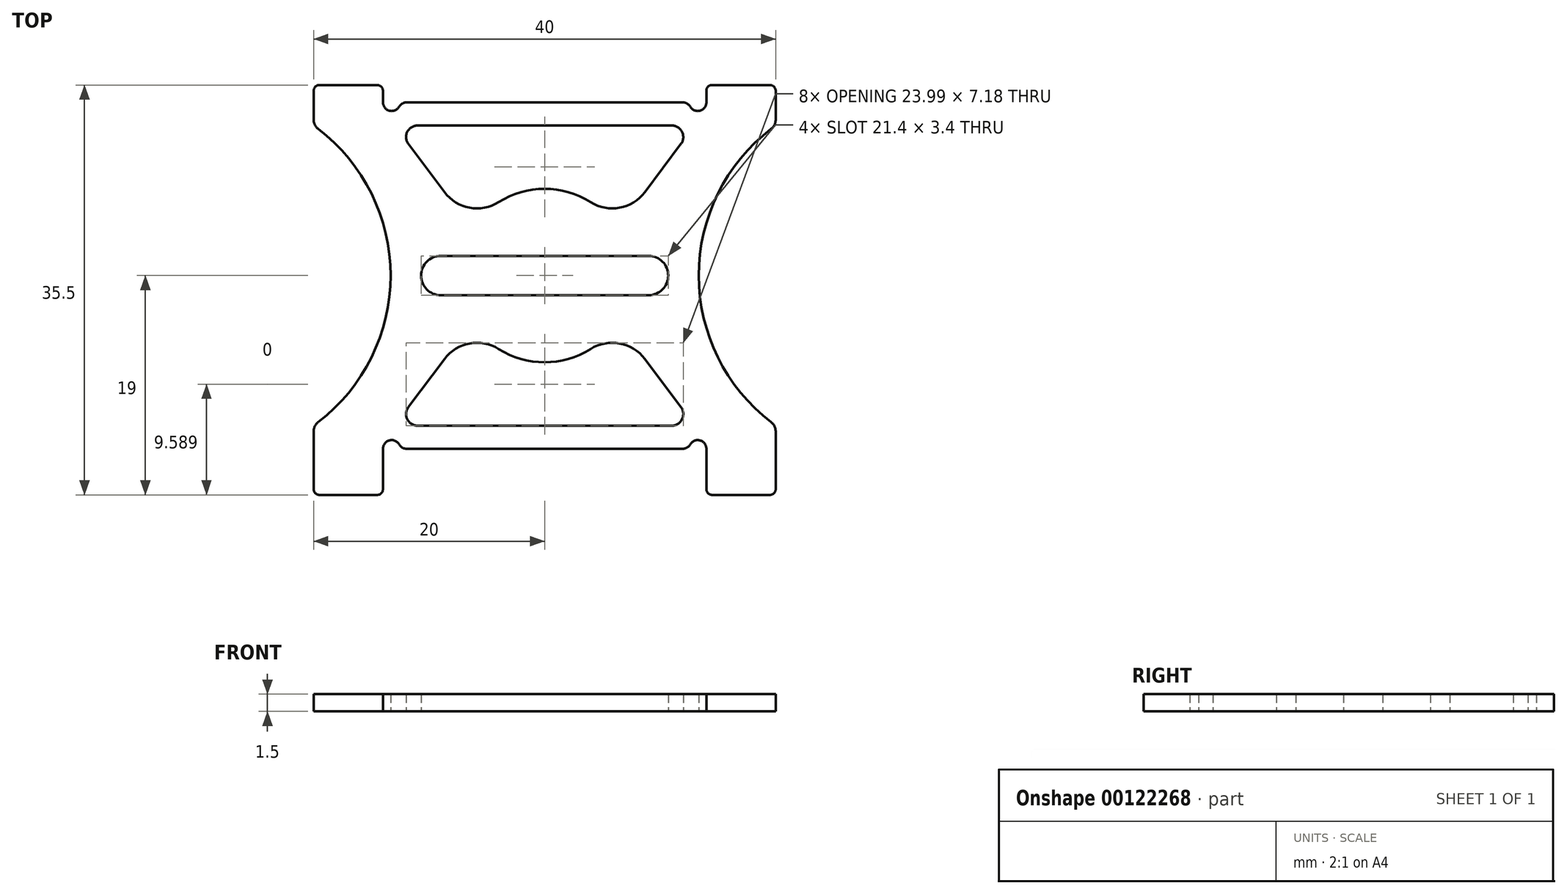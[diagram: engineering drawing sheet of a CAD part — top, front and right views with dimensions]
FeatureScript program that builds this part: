
annotation { "Feature Type Name" : "Feature", "Feature Type Description" : "" }
export const myFeature = defineFeature(function(context is Context, id is Id, definition is map)
    precondition{}
    {
        {
            var Q0;
            Q0=qCreatedBy(makeId("Top.planeOp"),FACE);
            var sketch = newSketch(context, id + "F0", { "sketchPlane" : qUnion([Q0])});
            skArc(sketch, "E0", {"start": v(19.6, 13.95) * mm, "mid": v(19.9, 14.3) * mm, "end": v(20, 14.74) * mm});
            skLineSegment(sketch, "E1", {"start": v(20, 14.74) * mm, "end": v(20, 17.25) * mm});
            skArc(sketch, "E2", {"start": v(20, 17.25) * mm, "mid": v(19.85, 17.6) * mm, "end": v(19.5, 17.75) * mm});
            skLineSegment(sketch, "E3", {"start": v(19.5, 17.75) * mm, "end": v(14.5, 17.75) * mm});
            skArc(sketch, "E4", {"start": v(14.5, 17.75) * mm, "mid": v(14.15, 17.6) * mm, "end": v(14, 17.25) * mm});
            skLineSegment(sketch, "E5", {"start": v(14, 17.25) * mm, "end": v(14, 16.25) * mm});
            skArc(sketch, "E6", {"start": v(12.6, 15.87) * mm, "mid": v(13.44, 15.53) * mm, "end": v(14, 16.25) * mm});
            skArc(sketch, "E7", {"start": v(12.6, 15.88) * mm, "mid": v(12.33, 16.15) * mm, "end": v(11.95, 16.25) * mm});
            skLineSegment(sketch, "E8", {"start": v(11.95, 16.25) * mm, "end": v(-11.95, 16.25) * mm});
            skArc(sketch, "E9", {"start": v(-11.95, 16.25) * mm, "mid": v(-12.33, 16.15) * mm, "end": v(-12.6, 15.88) * mm});
            skArc(sketch, "E10", {"start": v(-14, 16.25) * mm, "mid": v(-13.44, 15.53) * mm, "end": v(-12.6, 15.87) * mm});
            skLineSegment(sketch, "E11", {"start": v(-14, 16.25) * mm, "end": v(-14, 17.25) * mm});
            skArc(sketch, "E12", {"start": v(-14, 17.25) * mm, "mid": v(-14.15, 17.6) * mm, "end": v(-14.5, 17.75) * mm});
            skLineSegment(sketch, "E13", {"start": v(-14.5, 17.75) * mm, "end": v(-19.5, 17.75) * mm});
            skArc(sketch, "E14", {"start": v(-19.5, 17.75) * mm, "mid": v(-19.85, 17.6) * mm, "end": v(-20, 17.25) * mm});
            skLineSegment(sketch, "E15", {"start": v(-20, 17.25) * mm, "end": v(-20, 14.74) * mm});
            skArc(sketch, "E16", {"start": v(-20, 14.74) * mm, "mid": v(-19.9, 14.3) * mm, "end": v(-19.6, 13.95) * mm});
            skArc(sketch, "E17", {"start": v(-19.6, -11.45) * mm, "mid": v(-13.34, 1.25) * mm, "end": v(-19.6, 13.95) * mm});
            skArc(sketch, "E18", {"start": v(-19.6, -11.45) * mm, "mid": v(-19.9, -11.8) * mm, "end": v(-20, -12.24) * mm});
            skLineSegment(sketch, "E19", {"start": v(-20, -12.24) * mm, "end": v(-20, -17.25) * mm});
            skArc(sketch, "E20", {"start": v(-20, -17.25) * mm, "mid": v(-19.85, -17.6) * mm, "end": v(-19.5, -17.75) * mm});
            skLineSegment(sketch, "E21", {"start": v(-19.5, -17.75) * mm, "end": v(-14.5, -17.75) * mm});
            skArc(sketch, "E22", {"start": v(-14.5, -17.75) * mm, "mid": v(-14.15, -17.6) * mm, "end": v(-14, -17.25) * mm});
            skLineSegment(sketch, "E23", {"start": v(-14, -17.25) * mm, "end": v(-14, -13.75) * mm});
            skArc(sketch, "E24", {"start": v(-12.6, -13.37) * mm, "mid": v(-13.44, -13.03) * mm, "end": v(-14, -13.75) * mm});
            skArc(sketch, "E25", {"start": v(-12.6, -13.38) * mm, "mid": v(-12.33, -13.65) * mm, "end": v(-11.95, -13.75) * mm});
            skLineSegment(sketch, "E26", {"start": v(-11.95, -13.75) * mm, "end": v(11.95, -13.75) * mm});
            skArc(sketch, "E27", {"start": v(11.95, -13.75) * mm, "mid": v(12.33, -13.65) * mm, "end": v(12.6, -13.38) * mm});
            skArc(sketch, "E28", {"start": v(14, -13.75) * mm, "mid": v(13.44, -13.03) * mm, "end": v(12.6, -13.37) * mm});
            skLineSegment(sketch, "E29", {"start": v(14, -13.75) * mm, "end": v(14, -17.25) * mm});
            skArc(sketch, "E30", {"start": v(14, -17.25) * mm, "mid": v(14.15, -17.6) * mm, "end": v(14.5, -17.75) * mm});
            skLineSegment(sketch, "E31", {"start": v(14.5, -17.75) * mm, "end": v(19.5, -17.75) * mm});
            skArc(sketch, "E32", {"start": v(19.5, -17.75) * mm, "mid": v(19.85, -17.6) * mm, "end": v(20, -17.25) * mm});
            skLineSegment(sketch, "E33", {"start": v(20, -17.25) * mm, "end": v(20, -12.24) * mm});
            skArc(sketch, "E34", {"start": v(20, -12.24) * mm, "mid": v(19.9, -11.8) * mm, "end": v(19.6, -11.45) * mm});
            skArc(sketch, "E35", {"start": v(19.6, 13.95) * mm, "mid": v(13.34, 1.25) * mm, "end": v(19.6, -11.45) * mm});
            skLineSegment(sketch, "E36", {"start": v(9, -0.45) * mm, "end": v(-9, -0.45) * mm});
            skArc(sketch, "E37", {"start": v(9, -0.45) * mm, "mid": v(10.7, 1.25) * mm, "end": v(9, 2.95) * mm});
            skLineSegment(sketch, "E38", {"start": v(-9, 2.95) * mm, "end": v(9, 2.95) * mm});
            skArc(sketch, "E39", {"start": v(-9, 2.95) * mm, "mid": v(-10.7, 1.25) * mm, "end": v(-9, -0.45) * mm});
            skLineSegment(sketch, "E40", {"start": v(11, 14.25) * mm, "end": v(-11, 14.25) * mm});
            skArc(sketch, "E41", {"start": v(11.8, 12.65) * mm, "mid": v(11.9, 13.7) * mm, "end": v(11, 14.25) * mm});
            skLineSegment(sketch, "E42", {"start": v(8.67, 8.48) * mm, "end": v(11.8, 12.65) * mm});
            skArc(sketch, "E43", {"start": v(3.98, 7.61) * mm, "mid": v(6.5, 7.13) * mm, "end": v(8.67, 8.48) * mm});
            skArc(sketch, "E44", {"start": v(3.98, 7.61) * mm, "mid": v(0, 8.76) * mm, "end": v(-3.98, 7.61) * mm});
            skArc(sketch, "E45", {"start": v(-8.67, 8.48) * mm, "mid": v(-6.5, 7.13) * mm, "end": v(-3.98, 7.61) * mm});
            skLineSegment(sketch, "E46", {"start": v(-11.8, 12.65) * mm, "end": v(-8.67, 8.48) * mm});
            skArc(sketch, "E47", {"start": v(-11, 14.25) * mm, "mid": v(-11.9, 13.7) * mm, "end": v(-11.8, 12.65) * mm});
            skArc(sketch, "E48", {"start": v(-3.98, -5.11) * mm, "mid": v(-6.5, -4.63) * mm, "end": v(-8.67, -5.98) * mm});
            skArc(sketch, "E49", {"start": v(-3.98, -5.11) * mm, "mid": v(0, -6.26) * mm, "end": v(3.98, -5.11) * mm});
            skArc(sketch, "E50", {"start": v(8.67, -5.98) * mm, "mid": v(6.5, -4.63) * mm, "end": v(3.98, -5.11) * mm});
            skLineSegment(sketch, "E51", {"start": v(11.8, -10.15) * mm, "end": v(8.67, -5.98) * mm});
            skArc(sketch, "E52", {"start": v(11, -11.75) * mm, "mid": v(11.9, -11.2) * mm, "end": v(11.8, -10.15) * mm});
            skLineSegment(sketch, "E53", {"start": v(-11, -11.75) * mm, "end": v(11, -11.75) * mm});
            skArc(sketch, "E54", {"start": v(-11.8, -10.15) * mm, "mid": v(-11.9, -11.2) * mm, "end": v(-11, -11.75) * mm});
            skLineSegment(sketch, "E55", {"start": v(-8.67, -5.98) * mm, "end": v(-11.8, -10.15) * mm});
            skSolve(sketch);
        }
        {
            var Q0;
            Q0 = qSketchRegion(id + "F0", true);
            extrude(context, id + "F1", {"entities" : qUnion([Q0]), "depth" : 1.5 * mm});
        }
    });
